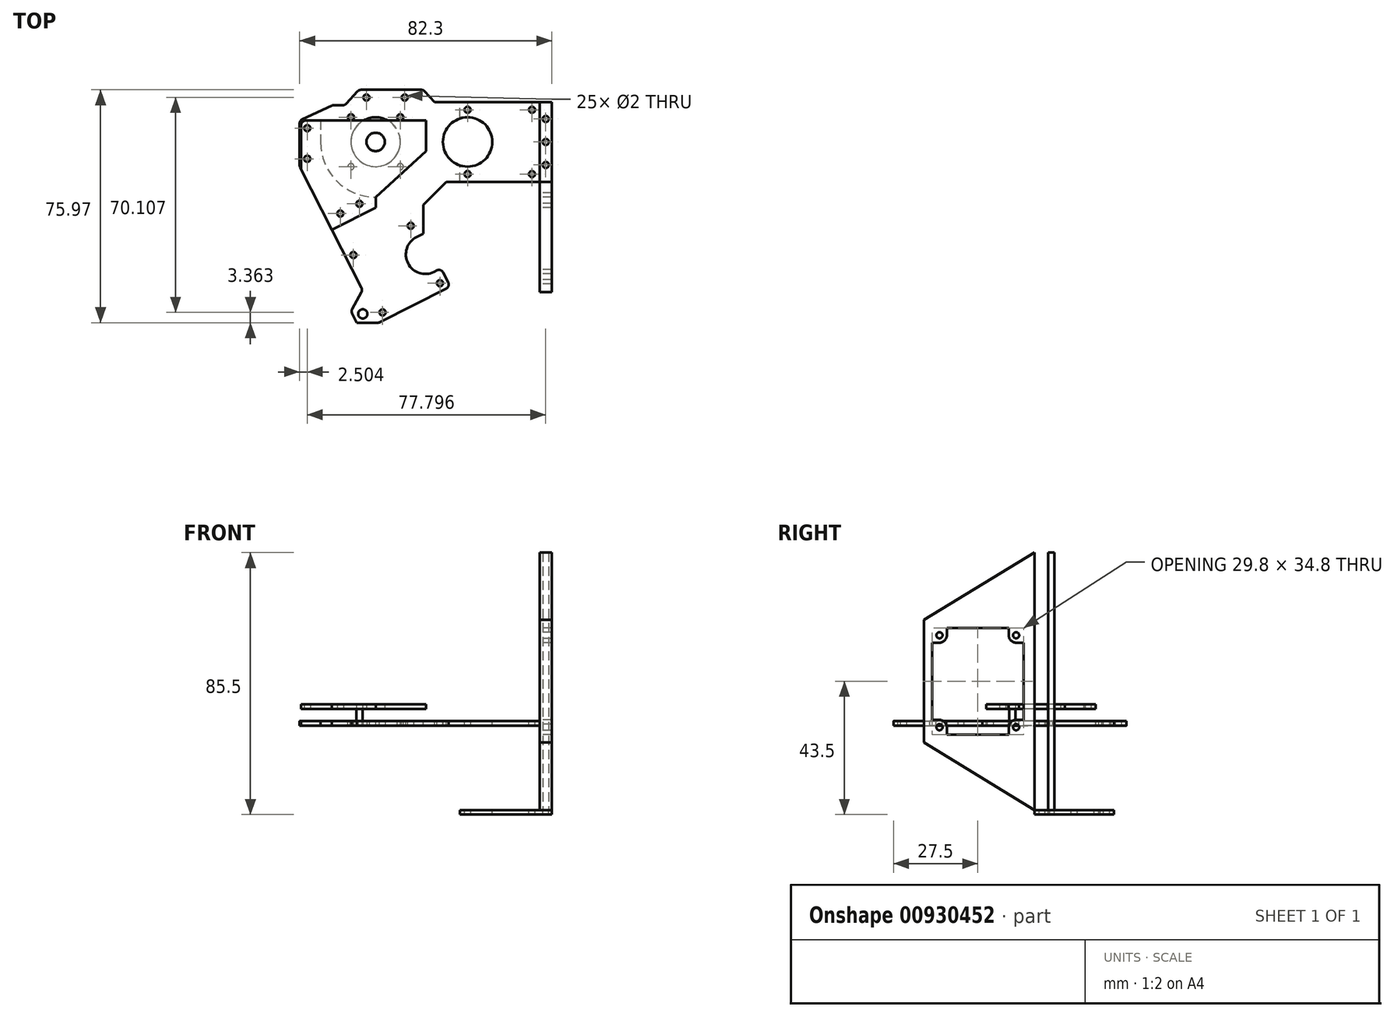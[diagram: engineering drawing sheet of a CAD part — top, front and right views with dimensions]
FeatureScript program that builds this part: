
annotation { "Feature Type Name" : "Feature", "Feature Type Description" : "" }
export const myFeature = defineFeature(function(context is Context, id is Id, definition is map)
    precondition{}
    {
        {
            var Q0;
            Q0=qCreatedBy(makeId("Top.planeOp"),FACE);
            var sketch = newSketch(context, id + "F0", { "sketchPlane" : qUnion([Q0])});
            skCircle(sketch, "E0", {"center": v(0, 0) * mm, "radius": 6.35 * mm, "construction": true});
            skCircle(sketch, "E1", {"center": v(0, 10.5) * mm, "radius": 1 * mm, "construction": true});
            skCircle(sketch, "E2", {"center": v(21, 10.5) * mm, "radius": 1 * mm, "construction": true});
            skCircle(sketch, "E3.MirrorC", {"center": v(0, -10.5) * mm, "radius": 1 * mm, "construction": true});
            skCircle(sketch, "E4.MirrorC", {"center": v(21, -10.5) * mm, "radius": 1 * mm, "construction": true});
            skLineSegment(sketch, "E5", {"start": v(0, 13) * mm, "end": v(-4, 13) * mm});
            skLineSegment(sketch, "E6", {"start": v(-14.8, 8) * mm, "end": v(-14.8, -7) * mm});
            skLineSegment(sketch, "E7", {"start": v(0, 0) * mm, "end": v(21, 0) * mm, "construction": true});
            skLineSegment(sketch, "E8.bottom", {"start": v(-2.5, 13) * mm, "end": v(23.5, 13) * mm, "construction": true});
            skLineSegment(sketch, "E8.top", {"start": v(-2.5, -13) * mm, "end": v(23.5, -13) * mm, "construction": true});
            skLineSegment(sketch, "E8.left", {"start": v(-2.5, 13) * mm, "end": v(-2.5, -13) * mm, "construction": true});
            skLineSegment(sketch, "E8.right", {"start": v(23.5, 13) * mm, "end": v(23.5, -13) * mm});
            skPoint(sketch, "E8.middle", {"position": v(10.5, 0) * mm});
            skLineSegment(sketch, "E9.bottom", {"start": v(21, -10.5) * mm, "end": v(0, -10.5) * mm, "construction": true});
            skLineSegment(sketch, "E9.top", {"start": v(21, 10.5) * mm, "end": v(0, 10.5) * mm, "construction": true});
            skLineSegment(sketch, "E9.left", {"start": v(21, -10.5) * mm, "end": v(21, 10.5) * mm, "construction": true});
            skLineSegment(sketch, "E9.right", {"start": v(0, -10.5) * mm, "end": v(0, 10.5) * mm, "construction": true});
            skLineSegment(sketch, "E10", {"start": v(21.44, -26.36) * mm, "end": v(2.73, -35.9) * mm, "construction": true});
            skLineSegment(sketch, "E11", {"start": v(2.73, -35.9) * mm, "end": v(7.5, -45.25) * mm, "construction": true});
            skLineSegment(sketch, "E12", {"start": v(7.5, -45.25) * mm, "end": v(26.21, -35.72) * mm, "construction": true});
            skLineSegment(sketch, "E13", {"start": v(26.21, -35.72) * mm, "end": v(21.44, -26.36) * mm, "construction": true});
            skLineSegment(sketch, "E14.MirrorCS", {"start": v(12.27, -54.6) * mm, "end": v(7.5, -45.25) * mm, "construction": true});
            skLineSegment(sketch, "E15.MirrorCS", {"start": v(30.98, -45.07) * mm, "end": v(12.27, -54.6) * mm, "construction": true});
            skLineSegment(sketch, "E16.MirrorCS", {"start": v(26.21, -35.72) * mm, "end": v(30.98, -45.07) * mm, "construction": true});
            skArc(sketch, "E17", {"start": v(2.62, -41.19) * mm, "mid": v(1.84, -48.13) * mm, "end": v(7.92, -51.59) * mm, "construction": true});
            skCircle(sketch, "E18", {"center": v(2.73, -35.9) * mm, "radius": 1 * mm});
            skCircle(sketch, "E19", {"center": v(21.44, -26.36) * mm, "radius": 1 * mm});
            skCircle(sketch, "E20", {"center": v(30.98, -45.07) * mm, "radius": 1 * mm});
            skCircle(sketch, "E21", {"center": v(12.27, -54.6) * mm, "radius": 1 * mm});
            skLineSegment(sketch, "E22", {"start": v(-0.63, -34.8) * mm, "end": v(22.54, -23) * mm, "construction": true});
            skLineSegment(sketch, "E23", {"start": v(22.54, -23) * mm, "end": v(34.34, -46.17) * mm, "construction": true});
            skLineSegment(sketch, "E24.MirrorCS", {"start": v(11.17, -57.97) * mm, "end": v(34.34, -46.17) * mm});
            skLineSegment(sketch, "E25", {"start": v(-0.63, -34.8) * mm, "end": v(11.17, -57.97) * mm, "construction": true});
            skLineSegment(sketch, "E26", {"start": v(11.17, -57.97) * mm, "end": v(34.34, -57.97) * mm});
            skLineSegment(sketch, "E27", {"start": v(0, 13) * mm, "end": v(34.34, 13) * mm});
            skLineSegment(sketch, "E28", {"start": v(34.34, 13) * mm, "end": v(34.34, -57.97) * mm, "construction": true});
            skPoint(sketch, "E29.orphan", {"position": v(0, -57.97) * mm});
            skLineSegment(sketch, "E30", {"start": v(11.17, -57.97) * mm, "end": v(-14.8, -7) * mm});
            skLineSegment(sketch, "E31", {"start": v(-14.8, 8) * mm, "end": v(-4, 13) * mm});
            skLineSegment(sketch, "E32", {"start": v(4.62, -39.6) * mm, "end": v(2.39, -40.73) * mm});
            skLineSegment(sketch, "E33.MirrorCS", {"start": v(10.38, -50.9) * mm, "end": v(8.16, -52.04) * mm});
            skArc(sketch, "E34.trimOffspring", {"start": v(10.38, -50.9) * mm, "mid": v(13.16, -42.37) * mm, "end": v(4.62, -39.6) * mm});
            skLineSegment(sketch, "E35", {"start": v(12.09, -31.13) * mm, "end": v(21.62, -49.84) * mm, "construction": true});
            skArc(sketch, "E36.MirrorCS", {"start": v(29.1, -41.38) * mm, "mid": v(20.55, -38.6) * mm, "end": v(23.33, -30.06) * mm});
            skLineSegment(sketch, "E37.MirrorCS", {"start": v(23.33, -30.06) * mm, "end": v(25.56, -28.93) * mm});
            skLineSegment(sketch, "E38.MirrorCS", {"start": v(29.1, -41.38) * mm, "end": v(31.32, -40.24) * mm});
            skArc(sketch, "E39", {"start": v(23.33, -30.06) * mm, "mid": v(20.55, -38.6) * mm, "end": v(29.1, -41.38) * mm});
            skLineSegment(sketch, "E40", {"start": v(11.17, -57.97) * mm, "end": v(3.88, -57.97) * mm});
            skLineSegment(sketch, "E41", {"start": v(3.88, -57.97) * mm, "end": v(1.98, -54.24) * mm});
            skLineSegment(sketch, "E42", {"start": v(1.98, -54.24) * mm, "end": v(5.73, -47.28) * mm});
            skCircle(sketch, "E43", {"center": v(5.79, -55.1) * mm, "radius": 1.5 * mm});
            skLineSegment(sketch, "E44", {"start": v(5.79, -55.1) * mm, "end": v(8.9, -53.51) * mm, "construction": true});
            skLineSegment(sketch, "E45", {"start": v(25.56, 13) * mm, "end": v(25.56, -28.93) * mm});
            skLineSegment(sketch, "E46", {"start": v(31.32, -40.24) * mm, "end": v(34.34, -46.17) * mm});
            skLineSegment(sketch, "E47", {"start": v(10.5, 10.5) * mm, "end": v(10.5, -10.5) * mm, "construction": true});
            skLineSegment(sketch, "E48", {"start": v(-14.8, 0.5) * mm, "end": v(-12.3, 0.5) * mm, "construction": true});
            skPoint(sketch, "E48.endSnap0", {"position": v(-14.8, 0.5) * mm});
            skCircle(sketch, "E49", {"center": v(-12.3, 5.5) * mm, "radius": 1 * mm});
            skCircle(sketch, "E50.MirrorC", {"center": v(-12.3, -4.5) * mm, "radius": 1 * mm});
            skLineSegment(sketch, "E51", {"start": v(30.11, -23.93) * mm, "end": v(25.56, -28.93) * mm});
            skLineSegment(sketch, "E52", {"start": v(0, 13) * mm, "end": v(4.56, 18) * mm});
            skLineSegment(sketch, "E53", {"start": v(4.56, 18) * mm, "end": v(25.56, 18) * mm});
            skLineSegment(sketch, "E54", {"start": v(25.56, 18) * mm, "end": v(25.56, 13) * mm, "construction": true});
            skCircle(sketch, "E55", {"center": v(19.5, 15.5) * mm, "radius": 1 * mm});
            skPoint(sketch, "E55.centerSnap0", {"position": v(25.56, 15.5) * mm});
            skCircle(sketch, "E56", {"center": v(7, 15.5) * mm, "radius": 1 * mm});
            skLineSegment(sketch, "E57", {"start": v(15.06, 18) * mm, "end": v(15.06, 13) * mm, "construction": true});
            skLineSegment(sketch, "E58.MirrorCS", {"start": v(30.11, 13) * mm, "end": v(25.56, 18) * mm});
            skLineSegment(sketch, "E59", {"start": v(30.11, 13) * mm, "end": v(30.11, -23.93) * mm});
            skLineSegment(sketch, "E60", {"start": v(23.5, -13) * mm, "end": v(23.5, -24.9) * mm});
            skLineSegment(sketch, "E61", {"start": v(23.5, -24.9) * mm, "end": v(25.56, -28.93) * mm});
            skLineSegment(sketch, "E62", {"start": v(23.5, 13) * mm, "end": v(23.5, 18) * mm});
            skCircle(sketch, "E63", {"center": v(10.5, 0) * mm, "radius": 8.75 * mm, "construction": true});
            skSolve(sketch);
        }
        {
            var Q0;
            {var subQ5=sQuery(id+"F0.wireOp",EDGE,"E5");Q0=makeQuery(id+"F0.imprint","IMPRINT",FACE,{"disambiguationData":[TD([[makeQuery(id+"F0.imprint","IMPRINT",EDGE,{"derivedFrom":subQ5}),1.0]])]});}
            var Q1;
            {var subQ3=sQuery(id+"F0.wireOp",EDGE,"E40");Q1=makeQuery(id+"F0.imprint","IMPRINT",FACE,{"disambiguationData":[TD([[makeQuery(id+"F0.imprint","IMPRINT",EDGE,{"derivedFrom":subQ3}),-1.0]])]});}
            var Q2;
            {var subQ1=sQuery(id+"F0.wireOp",EDGE,"E52");Q2=makeQuery(id+"F0.imprint","IMPRINT",FACE,{"disambiguationData":[TD([[makeQuery(id+"F0.imprint","IMPRINT",EDGE,{"derivedFrom":subQ1}),-1.0]])]});}
            var Q3;
            {var subQ0=sQuery(id+"F0.wireOp",EDGE,"E58.MirrorCS");Q3=makeQuery(id+"F0.imprint","IMPRINT",FACE,{"disambiguationData":[TD([[makeQuery(id+"F0.imprint","IMPRINT",EDGE,{"derivedFrom":subQ0}),1.0]])]});}
            var Q4;
            {var subQ2=sQuery(id+"F0.wireOp",EDGE,"E8.right");Q4=makeQuery(id+"F0.imprint","IMPRINT",FACE,{"disambiguationData":[TD([[makeQuery(id+"F0.imprint","IMPRINT",EDGE,{"derivedFrom":subQ2}),1.0]])]});}
            var Q5;
            {var subQ0=sQuery(id+"F0.wireOp",EDGE,"E45");Q5=makeQuery(id+"F0.imprint","IMPRINT",FACE,{"disambiguationData":[TD([[makeQuery(id+"F0.imprint","IMPRINT",EDGE,{"derivedFrom":subQ0}),1.0]])]});}
            var Q6;
            {var subQ0=sQuery(id+"F0.wireOp",EDGE,"E32");Q6=makeQuery(id+"F0.imprint","IMPRINT",FACE,{"disambiguationData":[TD([[makeQuery(id+"F0.imprint","IMPRINT",EDGE,{"derivedFrom":subQ0}),1.0]])]});}
            extrude(context, id + "F1", {"entities" : qUnion([Q0, Q1, Q2, Q3, Q4, Q5, Q6]), "oppositeDirection" : true, "depth" : 1.5 * mm, "offsetDistance" : 25 * mm});
        }
        {
            var Q0;
            Q0=makeQuery(id+"F1.opExtrude","SWEPT_EDGE",EDGE,{"disambiguationData":[OSD([sQuery(id+"F0.wireOp",EDGE,"E30"),sQuery(id+"F0.wireOp",EDGE,"E42")])]});
            var Q1;
            Q1=makeQuery(id+"F1.opExtrude","SWEPT_EDGE",EDGE,{"disambiguationData":[OSD([sQuery(id+"F0.wireOp",EDGE,"E41"),sQuery(id+"F0.wireOp",EDGE,"E42")])]});
            var Q2;
            Q2=makeQuery(id+"F1.opExtrude","SWEPT_EDGE",EDGE,{"disambiguationData":[OSD([sQuery(id+"F0.wireOp",EDGE,"E24.MirrorCS"),sQuery(id+"F0.wireOp",EDGE,"E30"),sQuery(id+"F0.wireOp",EDGE,"E40")])]});
            var Q3;
            Q3=makeQuery(id+"F1.opExtrude","SWEPT_EDGE",EDGE,{"disambiguationData":[OSD([sQuery(id+"F0.wireOp",EDGE,"E24.MirrorCS"),sQuery(id+"F0.wireOp",EDGE,"E46")])]});
            var Q4;
            Q4=makeQuery(id+"F1.opExtrude","SWEPT_EDGE",EDGE,{"disambiguationData":[OSD([sQuery(id+"F0.wireOp",EDGE,"E51"),sQuery(id+"F0.wireOp",EDGE,"E59")])]});
            var Q5;
            Q5=makeQuery(id+"F1.opExtrude","SWEPT_EDGE",EDGE,{"disambiguationData":[OSD([sQuery(id+"F0.wireOp",EDGE,"E38.MirrorCS"),sQuery(id+"F0.wireOp",EDGE,"E46")])]});
            var Q6;
            Q6=makeQuery(id+"F1.opExtrude","SWEPT_EDGE",EDGE,{"disambiguationData":[OSD([sQuery(id+"F0.wireOp",EDGE,"ywd1H7ED-kkhH-V58C-oYGJ-Jsg758ningq1.top"),sQuery(id+"F0.wireOp",EDGE,"E59")])]});
            var Q7;
            Q7=makeQuery(id+"F1.opExtrude","SWEPT_EDGE",EDGE,{"disambiguationData":[OSD([sQuery(id+"F0.wireOp",EDGE,"ywd1H7ED-kkhH-V58C-oYGJ-Jsg758ningq1.top"),sQuery(id+"F0.wireOp",EDGE,"ywd1H7ED-kkhH-V58C-oYGJ-Jsg758ningq1.right")])]});
            var Q8;
            Q8=makeQuery(id+"F1.opExtrude","SWEPT_EDGE",EDGE,{"disambiguationData":[OSD([sQuery(id+"F0.wireOp",EDGE,"ywd1H7ED-kkhH-V58C-oYGJ-Jsg758ningq1.bottom"),sQuery(id+"F0.wireOp",EDGE,"ywd1H7ED-kkhH-V58C-oYGJ-Jsg758ningq1.right")])]});
            var Q9;
            Q9=makeQuery(id+"F1.opExtrude","SWEPT_EDGE",EDGE,{"disambiguationData":[OSD([sQuery(id+"F0.wireOp",EDGE,"ywd1H7ED-kkhH-V58C-oYGJ-Jsg758ningq1.bottom"),sQuery(id+"F0.wireOp",EDGE,"E58.MirrorCS")])]});
            var Q10;
            Q10=makeQuery(id+"F1.opExtrude","SWEPT_EDGE",EDGE,{"disambiguationData":[OSD([sQuery(id+"F0.wireOp",EDGE,"E5"),sQuery(id+"F0.wireOp",EDGE,"E31")])]});
            var Q11;
            Q11=makeQuery(id+"F1.opExtrude","SWEPT_EDGE",EDGE,{"disambiguationData":[OSD([sQuery(id+"F0.wireOp",EDGE,"E6"),sQuery(id+"F0.wireOp",EDGE,"E31")])]});
            var Q12;
            Q12=makeQuery(id+"F1.opExtrude","SWEPT_EDGE",EDGE,{"disambiguationData":[OSD([sQuery(id+"F0.wireOp",EDGE,"E5"),sQuery(id+"F0.wireOp",EDGE,"E27"),sQuery(id+"F0.wireOp",EDGE,"E52")])]});
            var Q13;
            Q13=makeQuery(id+"F1.opExtrude","SWEPT_EDGE",EDGE,{"disambiguationData":[OSD([sQuery(id+"F0.wireOp",EDGE,"E6"),sQuery(id+"F0.wireOp",EDGE,"E30")])]});
            var Q14;
            {var subQ0=sQuery(id+"F0.wireOp",EDGE,"E52");Q14=makeQuery(id+"FCWeacQ4gwgFJkA_1.boolean.opBoolean","MERGE",EDGE,{"derivedFrom":[makeQuery(id+"F1.opExtrude","SWEPT_EDGE",EDGE,{"disambiguationData":[OSD([subQ0,sQuery(id+"F0.wireOp",EDGE,"E53")])]}),makeQuery(id+"FCWeacQ4gwgFJkA_1.opExtrude","SWEPT_EDGE",EDGE,{"disambiguationData":[OSD([subQ0,sQuery(id+"FNUyerKA4XAiE9j_1.wireOp",EDGE,"v8B43BBT-bsrC-yqZe-6j7p-HvjGZFhH99TZ.bottom"),sQuery(id+"FNUyerKA4XAiE9j_1.wireOp",EDGE,"v8B43BBT-bsrC-yqZe-6j7p-HvjGZFhH99TZ.left")])]})]});}
            var Q15;
            {var subQ0=sQuery(id+"F0.wireOp",EDGE,"E58.MirrorCS");Q15=makeQuery(id+"FCWeacQ4gwgFJkA_1.boolean.opBoolean","MERGE",EDGE,{"derivedFrom":[makeQuery(id+"F1.opExtrude","SWEPT_EDGE",EDGE,{"disambiguationData":[OSD([sQuery(id+"F0.wireOp",EDGE,"E53"),subQ0])]}),makeQuery(id+"FCWeacQ4gwgFJkA_1.opExtrude","SWEPT_EDGE",EDGE,{"disambiguationData":[OSD([subQ0,sQuery(id+"FNUyerKA4XAiE9j_1.wireOp",EDGE,"v8B43BBT-bsrC-yqZe-6j7p-HvjGZFhH99TZ.bottom"),sQuery(id+"FNUyerKA4XAiE9j_1.wireOp",EDGE,"v8B43BBT-bsrC-yqZe-6j7p-HvjGZFhH99TZ.right")])]})]});}
            fillet(context, id + "F2", {"entities" : qUnion([Q0, Q1, Q2, Q3, Q4, Q5, Q6, Q7, Q8, Q9, Q10, Q11, Q12, Q13, Q14, Q15]), "radius" : 1.5 * mm, "tangentPropagation" : true, "defaultsChanged" : false, "vertexSettings" : [], "allowEdgeOverflow" : false});
        }
        {
            var Q0;
            Q0=makeQuery(id+"F1.opExtrude","CAP_FACE",FACE,{"disambiguationData":[OSD([sQuery(id+"F0.wireOp",EDGE,"E5"),sQuery(id+"F0.wireOp",EDGE,"E6"),sQuery(id+"F0.wireOp",EDGE,"E18"),sQuery(id+"F0.wireOp",EDGE,"E19"),sQuery(id+"F0.wireOp",EDGE,"E20"),sQuery(id+"F0.wireOp",EDGE,"E21"),sQuery(id+"F0.wireOp",EDGE,"E24.MirrorCS"),sQuery(id+"F0.wireOp",EDGE,"E30"),sQuery(id+"F0.wireOp",EDGE,"E31"),sQuery(id+"F0.wireOp",EDGE,"E37.MirrorCS"),sQuery(id+"F0.wireOp",EDGE,"E38.MirrorCS"),sQuery(id+"F0.wireOp",EDGE,"E39"),sQuery(id+"F0.wireOp",EDGE,"E40"),sQuery(id+"F0.wireOp",EDGE,"E41"),sQuery(id+"F0.wireOp",EDGE,"E42"),sQuery(id+"F0.wireOp",EDGE,"E43"),sQuery(id+"F0.wireOp",EDGE,"E46"),sQuery(id+"F0.wireOp",EDGE,"E49"),sQuery(id+"F0.wireOp",EDGE,"E50.MirrorC"),sQuery(id+"F0.wireOp",EDGE,"E51"),sQuery(id+"F0.wireOp",EDGE,"E52"),sQuery(id+"F0.wireOp",EDGE,"E53"),sQuery(id+"F0.wireOp",EDGE,"E55"),sQuery(id+"F0.wireOp",EDGE,"E56"),sQuery(id+"F0.wireOp",EDGE,"E58.MirrorCS"),sQuery(id+"F0.wireOp",EDGE,"E59")])],"isStart":true});
            var sketch = newSketch(context, id + "F3", { "sketchPlane" : qUnion([Q0])});
            skCircle(sketch, "E64", {"center": v(10, 1) * mm, "radius": 8.05 * mm});
            skLineSegment(sketch, "E65", {"start": v(10, 1) * mm, "end": v(40, 1) * mm, "construction": true});
            skCircle(sketch, "E66", {"center": v(40, 1) * mm, "radius": 8.05 * mm});
            skLineSegment(sketch, "E67.bottom", {"start": v(40, 1) * mm, "end": v(61, 1) * mm, "construction": true});
            skLineSegment(sketch, "E67.top", {"start": v(40, 11.5) * mm, "end": v(61, 11.5) * mm, "construction": true});
            skLineSegment(sketch, "E67.left", {"start": v(40, 1) * mm, "end": v(40, 11.5) * mm, "construction": true});
            skLineSegment(sketch, "E67.right", {"start": v(61, 1) * mm, "end": v(61, 11.5) * mm, "construction": true});
            skLineSegment(sketch, "E68.MirrorCS", {"start": v(40, 1) * mm, "end": v(40, -9.5) * mm, "construction": true});
            skLineSegment(sketch, "E69.MirrorCS", {"start": v(40, -9.5) * mm, "end": v(61, -9.5) * mm, "construction": true});
            skLineSegment(sketch, "E70.MirrorCS", {"start": v(61, 1) * mm, "end": v(61, -9.5) * mm, "construction": true});
            skCircle(sketch, "E71", {"center": v(40, 11.5) * mm, "radius": 1 * mm});
            skCircle(sketch, "E72", {"center": v(61, 11.5) * mm, "radius": 1 * mm});
            skCircle(sketch, "E73.MirrorC", {"center": v(40, -9.5) * mm, "radius": 1 * mm});
            skCircle(sketch, "E74.MirrorC", {"center": v(61, -9.5) * mm, "radius": 1 * mm});
            skLineSegment(sketch, "E75", {"start": v(29.2, 14) * mm, "end": v(63.5, 14) * mm});
            skLineSegment(sketch, "E76", {"start": v(63.5, 14) * mm, "end": v(63.5, -12) * mm});
            skLineSegment(sketch, "E77", {"start": v(63.5, -12) * mm, "end": v(30.11, -22) * mm});
            skLineSegment(sketch, "E78.bottom", {"start": v(18.05, 9.05) * mm, "end": v(1.95, 9.05) * mm, "construction": true});
            skLineSegment(sketch, "E78.top", {"start": v(18.05, -7.05) * mm, "end": v(1.95, -7.05) * mm, "construction": true});
            skLineSegment(sketch, "E78.left", {"start": v(18.05, 9.05) * mm, "end": v(18.05, -7.05) * mm, "construction": true});
            skLineSegment(sketch, "E78.right", {"start": v(1.95, 9.05) * mm, "end": v(1.95, -7.05) * mm, "construction": true});
            skCircle(sketch, "E79", {"center": v(1.95, 9.05) * mm, "radius": 1 * mm});
            skCircle(sketch, "E80.1.0", {"center": v(1.95, -7.05) * mm, "radius": 1 * mm});
            skCircle(sketch, "E80.2.0", {"center": v(18.05, -7.05) * mm, "radius": 1 * mm});
            skCircle(sketch, "E81.1.3.0", {"center": v(18.05, 9.05) * mm, "radius": 1 * mm});
            skLineSegment(sketch, "E82", {"start": v(25.56, -28.93) * mm, "end": v(25.56, -12) * mm});
            skLineSegment(sketch, "E83", {"start": v(25.56, -12) * mm, "end": v(63.5, -12) * mm});
            skLineSegment(sketch, "E84", {"start": v(33.06, -12) * mm, "end": v(25.56, -19.5) * mm});
            skSolve(sketch);
        }
        {
            var Q0;
            Q0=makeQuery(id+"F3.imprint","IMPRINT",FACE,{"disambiguationData":[TD([[makeQuery(id+"F3.imprint","IMPRINT",EDGE,{"derivedFrom":sQuery(id+"F3.wireOp",EDGE,"E71")}),-1.0]])]});
            var Q1;
            {var subQ0=sQuery(id+"F3.wireOp",EDGE,"E84");var subQ1=sQuery(id+"F3.wireOp",EDGE,"E83");var subQ2=makeQuery(id+"F3.imprint","INTERSECT",VERTEX,{"derivedFrom":[subQ1,subQ0]});Q1=makeQuery(id+"F3.imprint","IMPRINT",FACE,{"disambiguationData":[TD([[makeQuery(id+"F3.imprint","IMPRINT",EDGE,{"disambiguationData":[TD([[subQ2,1.0]])],"derivedFrom":subQ1}),-1.0]])]});}
            var Q2;
            Q2=makeQuery(id+"F1.opExtrude","CAP_FACE",FACE,{"disambiguationData":[OSD([sQuery(id+"F0.wireOp",EDGE,"E5"),sQuery(id+"F0.wireOp",EDGE,"E6"),sQuery(id+"F0.wireOp",EDGE,"E18"),sQuery(id+"F0.wireOp",EDGE,"E19"),sQuery(id+"F0.wireOp",EDGE,"E20"),sQuery(id+"F0.wireOp",EDGE,"E21"),sQuery(id+"F0.wireOp",EDGE,"E24.MirrorCS"),sQuery(id+"F0.wireOp",EDGE,"E30"),sQuery(id+"F0.wireOp",EDGE,"E31"),sQuery(id+"F0.wireOp",EDGE,"E37.MirrorCS"),sQuery(id+"F0.wireOp",EDGE,"E38.MirrorCS"),sQuery(id+"F0.wireOp",EDGE,"E39"),sQuery(id+"F0.wireOp",EDGE,"E40"),sQuery(id+"F0.wireOp",EDGE,"E41"),sQuery(id+"F0.wireOp",EDGE,"E42"),sQuery(id+"F0.wireOp",EDGE,"E43"),sQuery(id+"F0.wireOp",EDGE,"E46"),sQuery(id+"F0.wireOp",EDGE,"E49"),sQuery(id+"F0.wireOp",EDGE,"E50.MirrorC"),sQuery(id+"F0.wireOp",EDGE,"E51"),sQuery(id+"F0.wireOp",EDGE,"E52"),sQuery(id+"F0.wireOp",EDGE,"E53"),sQuery(id+"F0.wireOp",EDGE,"E55"),sQuery(id+"F0.wireOp",EDGE,"E56"),sQuery(id+"F0.wireOp",EDGE,"E58.MirrorCS"),sQuery(id+"F0.wireOp",EDGE,"E59")])],"isStart":false});
            extrude(context, id + "F4", {"entities" : qUnion([Q0, Q1]), "operationType" : NewBodyOperationType.ADD, "endBound" : BoundingType.UP_TO_SURFACE, "oppositeDirection" : true, "depth" : 25 * mm, "endBoundEntityFace" : qUnion([Q2]), "offsetDistance" : 25 * mm});
        }
        {
            var Q0;
            Q0=makeQuery(id+"F3.imprint","IMPRINT",FACE,{"disambiguationData":[TD([[makeQuery(id+"F3.imprint","IMPRINT",EDGE,{"derivedFrom":sQuery(id+"F3.wireOp",EDGE,"E64")}),1.0]])]});
            var Q1;
            Q1=makeQuery(id+"F3.imprint","IMPRINT",FACE,{"disambiguationData":[TD([[makeQuery(id+"F3.imprint","IMPRINT",EDGE,{"derivedFrom":sQuery(id+"F3.wireOp",EDGE,"E79")}),1.0]])]});
            var Q2;
            Q2=makeQuery(id+"F3.imprint","IMPRINT",FACE,{"disambiguationData":[TD([[makeQuery(id+"F3.imprint","IMPRINT",EDGE,{"derivedFrom":sQuery(id+"F3.wireOp",EDGE,"E81.1.3.0")}),1.0]])]});
            var Q3;
            Q3=makeQuery(id+"F3.imprint","IMPRINT",FACE,{"disambiguationData":[TD([[makeQuery(id+"F3.imprint","IMPRINT",EDGE,{"derivedFrom":sQuery(id+"F3.wireOp",EDGE,"E80.2.0")}),1.0]])]});
            var Q4;
            Q4=makeQuery(id+"F3.imprint","IMPRINT",FACE,{"disambiguationData":[TD([[makeQuery(id+"F3.imprint","IMPRINT",EDGE,{"derivedFrom":sQuery(id+"F3.wireOp",EDGE,"E80.1.0")}),1.0]])]});
            var Q5;
            {var subQ0=sQuery(id+"F0.wireOp",EDGE,"E51");var subQ1=makeQuery(id+"F1.opExtrude","CAP_EDGE",EDGE,{"disambiguationData":[OSD([subQ0])],"isStart":true});Q5=makeQuery(id+"F3.imprint","IMPRINT",FACE,{"disambiguationData":[TD([[makeQuery(id+"F3.imprint","IMPRINT",EDGE,{"derivedFrom":subQ1}),-1.0]])]});}
            extrude(context, id + "F5", {"entities" : qUnion([Q0, Q1, Q2, Q3, Q4, Q5]), "operationType" : NewBodyOperationType.REMOVE, "endBound" : BoundingType.UP_TO_NEXT, "oppositeDirection" : true, "depth" : 25 * mm, "offsetDistance" : 25 * mm});
        }
        {
            var Q0;
            {var subQ0=sQuery(id+"F0.wireOp",EDGE,"E59");var subQ1=sQuery(id+"F0.wireOp",EDGE,"E58.MirrorCS");Q0=makeQuery(id+"F4.boolean.opBoolean","MERGE",FACE,{"derivedFrom":[makeQuery(id+"F1.opExtrude","CAP_FACE",FACE,{"disambiguationData":[OSD([sQuery(id+"F0.wireOp",EDGE,"E5"),sQuery(id+"F0.wireOp",EDGE,"E6"),sQuery(id+"F0.wireOp",EDGE,"E18"),sQuery(id+"F0.wireOp",EDGE,"E19"),sQuery(id+"F0.wireOp",EDGE,"E20"),sQuery(id+"F0.wireOp",EDGE,"E21"),sQuery(id+"F0.wireOp",EDGE,"E24.MirrorCS"),sQuery(id+"F0.wireOp",EDGE,"E30"),sQuery(id+"F0.wireOp",EDGE,"E31"),sQuery(id+"F0.wireOp",EDGE,"E37.MirrorCS"),sQuery(id+"F0.wireOp",EDGE,"E38.MirrorCS"),sQuery(id+"F0.wireOp",EDGE,"E39"),sQuery(id+"F0.wireOp",EDGE,"E40"),sQuery(id+"F0.wireOp",EDGE,"E41"),sQuery(id+"F0.wireOp",EDGE,"E42"),sQuery(id+"F0.wireOp",EDGE,"E43"),sQuery(id+"F0.wireOp",EDGE,"E46"),sQuery(id+"F0.wireOp",EDGE,"E49"),sQuery(id+"F0.wireOp",EDGE,"E50.MirrorC"),sQuery(id+"F0.wireOp",EDGE,"E51"),sQuery(id+"F0.wireOp",EDGE,"E52"),sQuery(id+"F0.wireOp",EDGE,"E53"),sQuery(id+"F0.wireOp",EDGE,"E55"),sQuery(id+"F0.wireOp",EDGE,"E56"),subQ1,subQ0])],"isStart":true}),makeQuery(id+"F4.opExtrude","CAP_FACE",FACE,{"disambiguationData":[OSD([subQ1,subQ0,sQuery(id+"F3.wireOp",EDGE,"E66"),sQuery(id+"F3.wireOp",EDGE,"E71"),sQuery(id+"F3.wireOp",EDGE,"E72"),sQuery(id+"F3.wireOp",EDGE,"E73.MirrorC"),sQuery(id+"F3.wireOp",EDGE,"E74.MirrorC"),sQuery(id+"F3.wireOp",EDGE,"E75"),sQuery(id+"F3.wireOp",EDGE,"E76"),sQuery(id+"F3.wireOp",EDGE,"E77")])],"isStart":true})]});}
            var sketch = newSketch(context, id + "F6", { "sketchPlane" : qUnion([Q0])});
            skLineSegment(sketch, "E85.bottom", {"start": v(-8, 8) * mm, "end": v(-12.8, 8) * mm});
            skLineSegment(sketch, "E85.top", {"start": v(-8, -7.98) * mm, "end": v(-14.3, -7.98) * mm, "construction": true});
            skLineSegment(sketch, "E85.left", {"start": v(-8, 8) * mm, "end": v(-8, 1) * mm});
            skLineSegment(sketch, "E85.right", {"start": v(-14.3, 6.5) * mm, "end": v(-14.3, -7.98) * mm});
            skCircle(sketch, "E86.0", {"center": v(-12.3, 5.5) * mm, "radius": 1 * mm});
            skCircle(sketch, "E87.0", {"center": v(-12.3, -4.5) * mm, "radius": 1 * mm});
            skCircle(sketch, "E88", {"center": v(10, 1) * mm, "radius": 16.5 * mm, "construction": true});
            skLineSegment(sketch, "E89", {"start": v(-14.3, -7.98) * mm, "end": v(-4.26, -27.68) * mm});
            skLineSegment(sketch, "E90", {"start": v(-4.26, -27.68) * mm, "end": v(10, -20.4) * mm});
            skCircle(sketch, "E91.0", {"center": v(2.73, -35.9) * mm, "radius": 1 * mm, "construction": true});
            skArc(sketch, "E92", {"start": v(-8, 1) * mm, "mid": v(-2.73, -11.73) * mm, "end": v(10, -17) * mm});
            skPoint(sketch, "E93", {"position": v(10, -15.5) * mm});
            skLineSegment(sketch, "E94", {"start": v(10, -17) * mm, "end": v(10, -20.4) * mm});
            skPoint(sketch, "E95.orphan", {"position": v(10, 19) * mm});
            skPoint(sketch, "E96.visualSharp", {"position": v(-14.3, 8) * mm});
            skArc(sketch, "E96.filletArc", {"start": v(-12.8, 8) * mm, "mid": v(-13.86, 7.56) * mm, "end": v(-14.3, 6.5) * mm});
            skSolve(sketch);
        }
        {
            var Q0;
            Q0 = qSketchRegion(id + "F6", true);
            extrude(context, id + "F7", {"entities" : qUnion([Q0]), "depth" : 4 * mm, "offsetDistance" : 25 * mm});
        }
        {
            var Q0;
            Q0=makeQuery(id+"F7.opExtrude","CAP_FACE",FACE,{"disambiguationData":[OSD([sQuery(id+"F6.wireOp",EDGE,"E85.bottom"),sQuery(id+"F6.wireOp",EDGE,"E85.left"),sQuery(id+"F6.wireOp",EDGE,"E85.right"),sQuery(id+"F6.wireOp",EDGE,"E86.0"),sQuery(id+"F6.wireOp",EDGE,"E87.0"),sQuery(id+"F6.wireOp",EDGE,"E89"),sQuery(id+"F6.wireOp",EDGE,"E90"),sQuery(id+"F6.wireOp",EDGE,"E92"),sQuery(id+"F6.wireOp",EDGE,"E94"),sQuery(id+"F6.wireOp",EDGE,"E96.filletArc")])],"isStart":false});
            var sketch = newSketch(context, id + "F8", { "sketchPlane" : qUnion([Q0])});
            skLineSegment(sketch, "E97.3", {"start": v(-4.26, -27.68) * mm, "end": v(-14.3, -7.98) * mm});
            skArc(sketch, "E97.4", {"start": v(-8, 1) * mm, "mid": v(-2.73, -11.73) * mm, "end": v(10, -17) * mm});
            skLineSegment(sketch, "E97.10", {"start": v(-14.3, 6.5) * mm, "end": v(-14.3, -7.98) * mm});
            skCircle(sketch, "E97.11", {"center": v(-12.3, 5.5) * mm, "radius": 1 * mm});
            skLineSegment(sketch, "E97.12", {"start": v(-8, 8) * mm, "end": v(-12.8, 8) * mm});
            skLineSegment(sketch, "E97.13", {"start": v(-8, 8) * mm, "end": v(-8, 1) * mm, "construction": true});
            skCircle(sketch, "E97.14", {"center": v(-12.3, -4.5) * mm, "radius": 1 * mm});
            skLineSegment(sketch, "E97.15", {"start": v(-4.26, -27.68) * mm, "end": v(-14.3, -7.98) * mm});
            skLineSegment(sketch, "E97.16", {"start": v(-4.26, -27.68) * mm, "end": v(10, -20.4) * mm});
            skArc(sketch, "E97.17", {"start": v(-8, 1) * mm, "mid": v(-2.73, -11.73) * mm, "end": v(10, -17) * mm, "construction": true});
            skLineSegment(sketch, "E97.18", {"start": v(10, -17) * mm, "end": v(10, -20.4) * mm});
            skArc(sketch, "E97.19", {"start": v(-12.8, 8) * mm, "mid": v(-13.86, 7.56) * mm, "end": v(-14.3, 6.5) * mm});
            skCircle(sketch, "E97.24", {"center": v(-12.3, -4.5) * mm, "radius": 1 * mm});
            skLineSegment(sketch, "E97.34", {"start": v(-8, 8) * mm, "end": v(-12.8, 8) * mm});
            skLineSegment(sketch, "E97.35", {"start": v(-8, 8) * mm, "end": v(-8, 1) * mm});
            skLineSegment(sketch, "E97.36", {"start": v(-14.3, 6.5) * mm, "end": v(-14.3, -7.98) * mm});
            skLineSegment(sketch, "E97.37", {"start": v(-4.26, -27.68) * mm, "end": v(10, -20.4) * mm});
            skLineSegment(sketch, "E97.38", {"start": v(10, -17) * mm, "end": v(10, -20.4) * mm});
            skArc(sketch, "E97.39", {"start": v(-12.8, 8) * mm, "mid": v(-13.86, 7.56) * mm, "end": v(-14.3, 6.5) * mm});
            skCircle(sketch, "E97.41", {"center": v(-12.3, 5.5) * mm, "radius": 1 * mm});
            skCircle(sketch, "E97.42", {"center": v(-12.3, -4.5) * mm, "radius": 1 * mm});
            skCircle(sketch, "E97.43", {"center": v(-12.3, -4.5) * mm, "radius": 1 * mm});
            skCircle(sketch, "E97.44", {"center": v(-12.3, 5.5) * mm, "radius": 1 * mm});
            skCircle(sketch, "E97.45", {"center": v(-12.3, 5.5) * mm, "radius": 1 * mm});
            skCircle(sketch, "E98", {"center": v(10, 1) * mm, "radius": 3 * mm});
            skLineSegment(sketch, "E99", {"start": v(-8, 8) * mm, "end": v(26.5, 8) * mm});
            skLineSegment(sketch, "E100", {"start": v(26.5, 8) * mm, "end": v(26.5, -2) * mm});
            skLineSegment(sketch, "E101", {"start": v(26.5, -2) * mm, "end": v(10, -17) * mm});
            skLineSegment(sketch, "E102", {"start": v(-5.85, -24.56) * mm, "end": v(9.03, -16.97) * mm, "construction": true});
            skLineSegment(sketch, "E103", {"start": v(1.6, -20.77) * mm, "end": v(3.18, -23.88) * mm, "construction": true});
            skCircle(sketch, "E104", {"center": v(-1.53, -22.35) * mm, "radius": 1 * mm});
            skCircle(sketch, "E105.MirrorC", {"center": v(4.7, -19.18) * mm, "radius": 1 * mm});
            skSolve(sketch);
        }
        {
            var Q0;
            Q0 = qSketchRegion(id + "F8", true);
            extrude(context, id + "F9", {"entities" : qUnion([Q0]), "depth" : 1.5 * mm, "offsetDistance" : 25 * mm});
        }
        {
            var Q0;
            Q0=makeQuery(id+"F7.opExtrude","SWEPT_FACE",FACE,{"disambiguationData":[OSD([sQuery(id+"F6.wireOp",EDGE,"E89")])]});
            var sketch = newSketch(context, id + "F10", { "sketchPlane" : qUnion([Q0])});
            skLineSegment(sketch, "E106", {"start": v(0.62, 2) * mm, "end": v(22.72, 2) * mm, "construction": true});
            skLineSegment(sketch, "E107", {"start": v(11.67, 4) * mm, "end": v(11.67, 0) * mm, "construction": true});
            skCircle(sketch, "E108", {"center": v(16.22, 2) * mm, "radius": 0.8 * mm});
            skCircle(sketch, "E109.1.0.0", {"center": v(9.72, 2) * mm, "radius": 0.8 * mm});
            skCircle(sketch, "E109.2.0.0", {"center": v(3.22, 2) * mm, "radius": 0.8 * mm});
            skLineSegment(sketch, "E109.direction1", {"start": v(16.22, 2) * mm, "end": v(9.72, 2) * mm, "construction": true});
            skSolve(sketch);
        }
        {
            var Q0;
            Q0 = qSketchRegion(id + "F10", true);
            extrude(context, id + "F11", {"entities" : qUnion([Q0]), "operationType" : NewBodyOperationType.REMOVE, "oppositeDirection" : true, "depth" : 4 * mm, "offsetDistance" : 25 * mm});
        }
        {
            var Q0;
            Q0=makeQuery(id+"F8.imprint","IMPRINT",FACE,{"disambiguationData":[TD([[makeQuery(id+"F8.imprint","IMPRINT",EDGE,{"derivedFrom":sQuery(id+"F8.wireOp",EDGE,"E105.MirrorC")}),-1.0]])]});
            var Q1;
            Q1=makeQuery(id+"F8.imprint","IMPRINT",FACE,{"disambiguationData":[TD([[makeQuery(id+"F8.imprint","IMPRINT",EDGE,{"derivedFrom":sQuery(id+"F8.wireOp",EDGE,"E104")}),1.0]])]});
            extrude(context, id + "F12", {"entities" : qUnion([Q0, Q1]), "operationType" : NewBodyOperationType.REMOVE, "endBound" : BoundingType.THROUGH_ALL, "oppositeDirection" : true, "depth" : 25 * mm, "offsetDistance" : 25 * mm});
        }
        {
            var Q0;
            Q0=makeQuery(id+"F4.opExtrude","SWEPT_FACE",FACE,{"disambiguationData":[OSD([sQuery(id+"F3.wireOp",EDGE,"E76")])]});
            var sketch = newSketch(context, id + "F13", { "sketchPlane" : qUnion([Q0])});
            skLineSegment(sketch, "E110.bottom", {"start": v(14, -29) * mm, "end": v(-47.97, -29) * mm});
            skLineSegment(sketch, "E110.top", {"start": v(14, 55) * mm, "end": v(-47.97, 55) * mm});
            skLineSegment(sketch, "E110.left", {"start": v(14, -29) * mm, "end": v(14, 55) * mm});
            skLineSegment(sketch, "E110.right", {"start": v(-47.97, -29) * mm, "end": v(-47.97, 55) * mm});
            skPoint(sketch, "E110.middle", {"position": v(-16.98, 13) * mm});
            skLineSegment(sketch, "E111.bottom", {"start": v(-17.97, 28) * mm, "end": v(-42.97, 28) * mm, "construction": true});
            skLineSegment(sketch, "E111.top", {"start": v(-17.97, -2) * mm, "end": v(-42.97, -2) * mm, "construction": true});
            skLineSegment(sketch, "E111.left", {"start": v(-17.97, 28) * mm, "end": v(-17.97, -2) * mm, "construction": true});
            skLineSegment(sketch, "E111.right", {"start": v(-42.97, 28) * mm, "end": v(-42.97, -2) * mm, "construction": true});
            skPoint(sketch, "E111.middle", {"position": v(-30.47, 13) * mm});
            skCircle(sketch, "E112", {"center": v(-17.97, 28) * mm, "radius": 1 * mm});
            skCircle(sketch, "E113", {"center": v(-17.97, -2) * mm, "radius": 1 * mm});
            skCircle(sketch, "E114", {"center": v(-42.97, 28) * mm, "radius": 1 * mm});
            skCircle(sketch, "E115", {"center": v(-42.97, -2) * mm, "radius": 1 * mm});
            skArc(sketch, "E116", {"start": v(-42.97, 25.6) * mm, "mid": v(-41.27, 26.3) * mm, "end": v(-40.57, 28) * mm});
            skArc(sketch, "E117", {"start": v(-20.37, 28) * mm, "mid": v(-19.67, 26.3) * mm, "end": v(-17.97, 25.6) * mm});
            skArc(sketch, "E118", {"start": v(-17.97, 0.4) * mm, "mid": v(-19.67, -0.3) * mm, "end": v(-20.37, -2) * mm});
            skArc(sketch, "E119", {"start": v(-40.57, -2) * mm, "mid": v(-41.27, -0.3) * mm, "end": v(-42.97, 0.4) * mm});
            skLineSegment(sketch, "E120", {"start": v(-20.37, 28) * mm, "end": v(-20.37, 30.4) * mm});
            skPoint(sketch, "E121", {"position": v(-17.97, 30.4) * mm});
            skLineSegment(sketch, "E122", {"start": v(-20.37, 30.4) * mm, "end": v(-30.47, 30.4) * mm});
            skPoint(sketch, "E122.endSnap0", {"position": v(-30.47, 28) * mm});
            skLineSegment(sketch, "E123", {"start": v(-30.47, 28) * mm, "end": v(-30.47, -2) * mm, "construction": true});
            skLineSegment(sketch, "E124", {"start": v(-17.97, 13) * mm, "end": v(-42.97, 13) * mm, "construction": true});
            skLineSegment(sketch, "E125.MirrorCS", {"start": v(-40.57, 30.4) * mm, "end": v(-30.47, 30.4) * mm});
            skLineSegment(sketch, "E126.MirrorCS", {"start": v(-40.57, 28) * mm, "end": v(-40.57, 30.4) * mm});
            skLineSegment(sketch, "E127.MirrorCS", {"start": v(-20.37, -2) * mm, "end": v(-20.37, -4.4) * mm});
            skLineSegment(sketch, "E128.MirrorCS", {"start": v(-20.37, -4.4) * mm, "end": v(-30.47, -4.4) * mm});
            skLineSegment(sketch, "E129.MirrorCS", {"start": v(-40.57, -4.4) * mm, "end": v(-30.47, -4.4) * mm});
            skLineSegment(sketch, "E130.MirrorCS", {"start": v(-40.57, -2) * mm, "end": v(-40.57, -4.4) * mm});
            skPoint(sketch, "E131", {"position": v(-45.37, 28) * mm});
            skLineSegment(sketch, "E132", {"start": v(-42.97, 25.6) * mm, "end": v(-45.37, 25.6) * mm});
            skLineSegment(sketch, "E133", {"start": v(-45.37, 25.6) * mm, "end": v(-45.37, 13) * mm});
            skLineSegment(sketch, "E134.MirrorCS", {"start": v(-45.37, 0.4) * mm, "end": v(-45.37, 13) * mm});
            skLineSegment(sketch, "E135.MirrorCS", {"start": v(-42.97, 0.4) * mm, "end": v(-45.37, 0.4) * mm});
            skLineSegment(sketch, "E136.MirrorCS", {"start": v(-17.97, 25.6) * mm, "end": v(-15.57, 25.6) * mm});
            skLineSegment(sketch, "E137.MirrorCS", {"start": v(-15.57, 25.6) * mm, "end": v(-15.57, 13) * mm});
            skLineSegment(sketch, "E138.MirrorCS", {"start": v(-15.57, 0.4) * mm, "end": v(-15.57, 13) * mm});
            skLineSegment(sketch, "E139.MirrorCS", {"start": v(-17.97, 0.4) * mm, "end": v(-15.57, 0.4) * mm});
            skLineSegment(sketch, "E140", {"start": v(-47.97, -7) * mm, "end": v(-12, -29) * mm});
            skLineSegment(sketch, "E141.MirrorCS", {"start": v(-47.97, 33) * mm, "end": v(-12, 55) * mm});
            skSolve(sketch);
        }
        {
            var Q0;
            {var subQ1=sQuery(id+"F3.wireOp",EDGE,"E76");var subQ2=makeQuery(id+"F4.opExtrude","CAP_EDGE",EDGE,{"disambiguationData":[OSD([subQ1])],"isStart":true});Q0=makeQuery(id+"F13.imprint","IMPRINT",FACE,{"disambiguationData":[TD([[makeQuery(id+"F13.imprint","IMPRINT",EDGE,{"derivedFrom":subQ2}),1.0]])]});}
            var Q1;
            Q1=makeQuery(id+"F13.imprint","IMPRINT",FACE,{"disambiguationData":[TD([[makeQuery(id+"F13.imprint","IMPRINT",EDGE,{"derivedFrom":sQuery(id+"F13.wireOp",EDGE,"E112")}),-1.0]])]});
            extrude(context, id + "F14", {"entities" : qUnion([Q0, Q1]), "depth" : 4 * mm, "offsetDistance" : 25 * mm});
        }
        {
            var Q0;
            Q0=makeQuery(id+"F14.opExtrude","SWEPT_FACE",FACE,{"disambiguationData":[OSD([sQuery(id+"F13.wireOp",EDGE,"E110.bottom")])]});
            var sketch = newSketch(context, id + "F15", { "sketchPlane" : qUnion([Q0])});
            skPoint(sketch, "E142.0", {"position": v(33.06, 12) * mm});
            skPoint(sketch, "E143.0", {"position": v(29.2, -14) * mm});
            skLineSegment(sketch, "E144.bottom", {"start": v(67.5, 12) * mm, "end": v(37.5, 12) * mm});
            skLineSegment(sketch, "E144.top", {"start": v(67.5, -14) * mm, "end": v(37.5, -14) * mm});
            skLineSegment(sketch, "E144.left", {"start": v(67.5, 12) * mm, "end": v(67.5, -14) * mm});
            skLineSegment(sketch, "E144.right", {"start": v(37.5, 12) * mm, "end": v(37.5, 7.05) * mm});
            skCircle(sketch, "E145.0", {"center": v(61, -11.5) * mm, "radius": 1 * mm});
            skCircle(sketch, "E146.0", {"center": v(40, -11.5) * mm, "radius": 1 * mm});
            skCircle(sketch, "E147.0", {"center": v(61, 9.5) * mm, "radius": 1 * mm});
            skCircle(sketch, "E148.0", {"center": v(40, 9.5) * mm, "radius": 1 * mm});
            skArc(sketch, "E149.0", {"start": v(40, -9.05) * mm, "mid": v(48.05, -1) * mm, "end": v(40, 7.05) * mm});
            skLineSegment(sketch, "E150", {"start": v(40, -9.05) * mm, "end": v(37.5, -9.05) * mm});
            skLineSegment(sketch, "E151", {"start": v(40, 7.05) * mm, "end": v(37.5, 7.05) * mm});
            skLineSegment(sketch, "E152.trimOffspring", {"start": v(37.5, -9.05) * mm, "end": v(37.5, -14) * mm});
            skLineSegment(sketch, "E153", {"start": v(40, -1) * mm, "end": v(67.5, -1) * mm, "construction": true});
            skLineSegment(sketch, "E154", {"start": v(65.5, -14) * mm, "end": v(65.5, 12) * mm, "construction": true});
            skCircle(sketch, "E155", {"center": v(65.5, -8.5) * mm, "radius": 1 * mm});
            skCircle(sketch, "E156", {"center": v(65.5, -1) * mm, "radius": 1 * mm});
            skCircle(sketch, "E157.MirrorC", {"center": v(65.5, 6.5) * mm, "radius": 1 * mm});
            skSolve(sketch);
        }
        {
            var Q0;
            Q0 = qSketchRegion(id + "F15", true);
            extrude(context, id + "F16", {"entities" : qUnion([Q0]), "depth" : 1.5 * mm, "offsetDistance" : 25 * mm});
        }
        {
            var Q0;
            Q0=makeQuery(id+"F15.imprint","IMPRINT",FACE,{"disambiguationData":[TD([[makeQuery(id+"F15.imprint","IMPRINT",EDGE,{"derivedFrom":sQuery(id+"F15.wireOp",EDGE,"E155")}),1.0]])]});
            var Q1;
            Q1=makeQuery(id+"F15.imprint","IMPRINT",FACE,{"disambiguationData":[TD([[makeQuery(id+"F15.imprint","IMPRINT",EDGE,{"derivedFrom":sQuery(id+"F15.wireOp",EDGE,"E156")}),1.0]])]});
            var Q2;
            Q2=makeQuery(id+"F15.imprint","IMPRINT",FACE,{"disambiguationData":[TD([[makeQuery(id+"F15.imprint","IMPRINT",EDGE,{"derivedFrom":sQuery(id+"F15.wireOp",EDGE,"E157.MirrorC")}),-1.0]])]});
            extrude(context, id + "F17", {"entities" : qUnion([Q0, Q1, Q2]), "operationType" : NewBodyOperationType.REMOVE, "endBound" : BoundingType.THROUGH_ALL, "oppositeDirection" : true, "depth" : 25 * mm, "offsetDistance" : 25 * mm});
        }
    });
